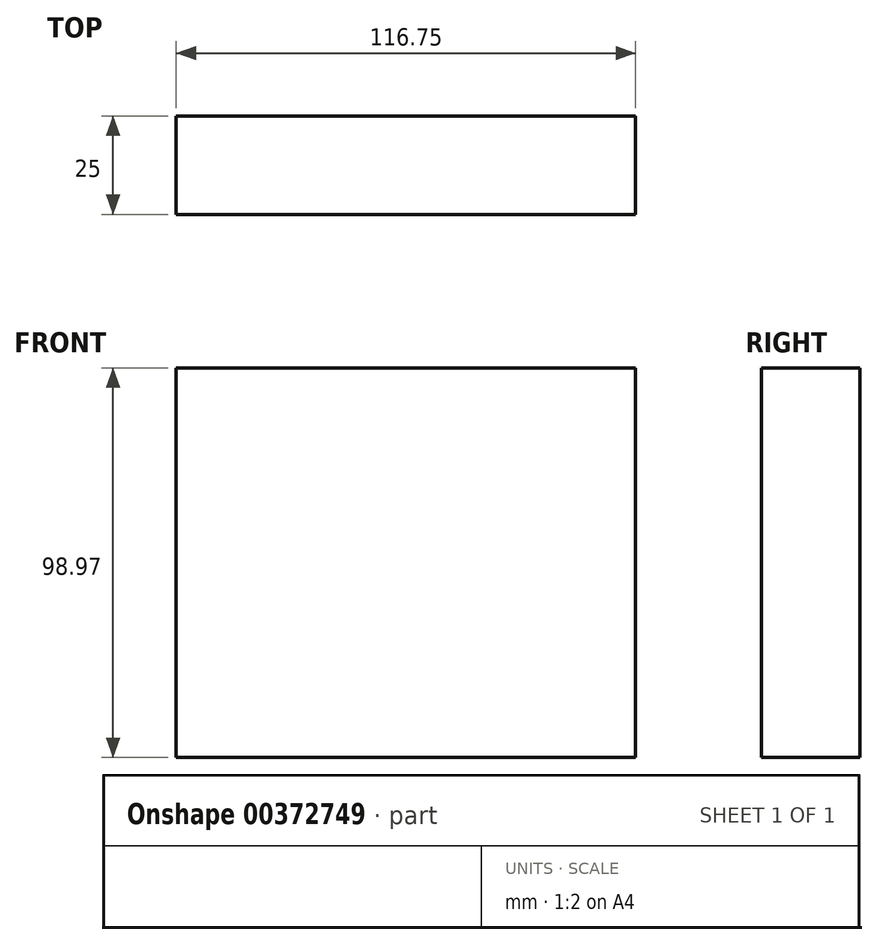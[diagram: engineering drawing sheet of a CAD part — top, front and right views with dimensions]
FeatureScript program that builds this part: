
annotation { "Feature Type Name" : "Feature", "Feature Type Description" : "" }
export const myFeature = defineFeature(function(context is Context, id is Id, definition is map)
    precondition{}
    {
        {
            var Q0;
            Q0=qCreatedBy(makeId("Front.planeOp"),FACE);
            var sketch = newSketch(context, id + "F0", { "sketchPlane" : qUnion([Q0])});
            skLineSegment(sketch, "E0.bottom", {"start": v(-60.72, 98.97) * mm, "end": v(56.03, 98.97) * mm});
            skLineSegment(sketch, "E0.top", {"start": v(-60.72, 0) * mm, "end": v(56.03, 0) * mm});
            skLineSegment(sketch, "E0.left", {"start": v(-60.72, 98.97) * mm, "end": v(-60.72, 0) * mm});
            skLineSegment(sketch, "E0.right", {"start": v(56.03, 98.97) * mm, "end": v(56.03, 0) * mm});
            skSolve(sketch);
        }
        {
            var Q0;
            Q0=makeQuery(id+"F0.imprint","IMPRINT",FACE,{"disambiguationData":[TD([[makeQuery(id+"F0.imprint","IMPRINT",EDGE,{"derivedFrom":sQuery(id+"F0.wireOp",EDGE,"E0.bottom")}),-1.0]])]});
            extrude(context, id + "F1", {"entities" : qUnion([Q0]), "depth" : 25 * mm});
        }
    });
